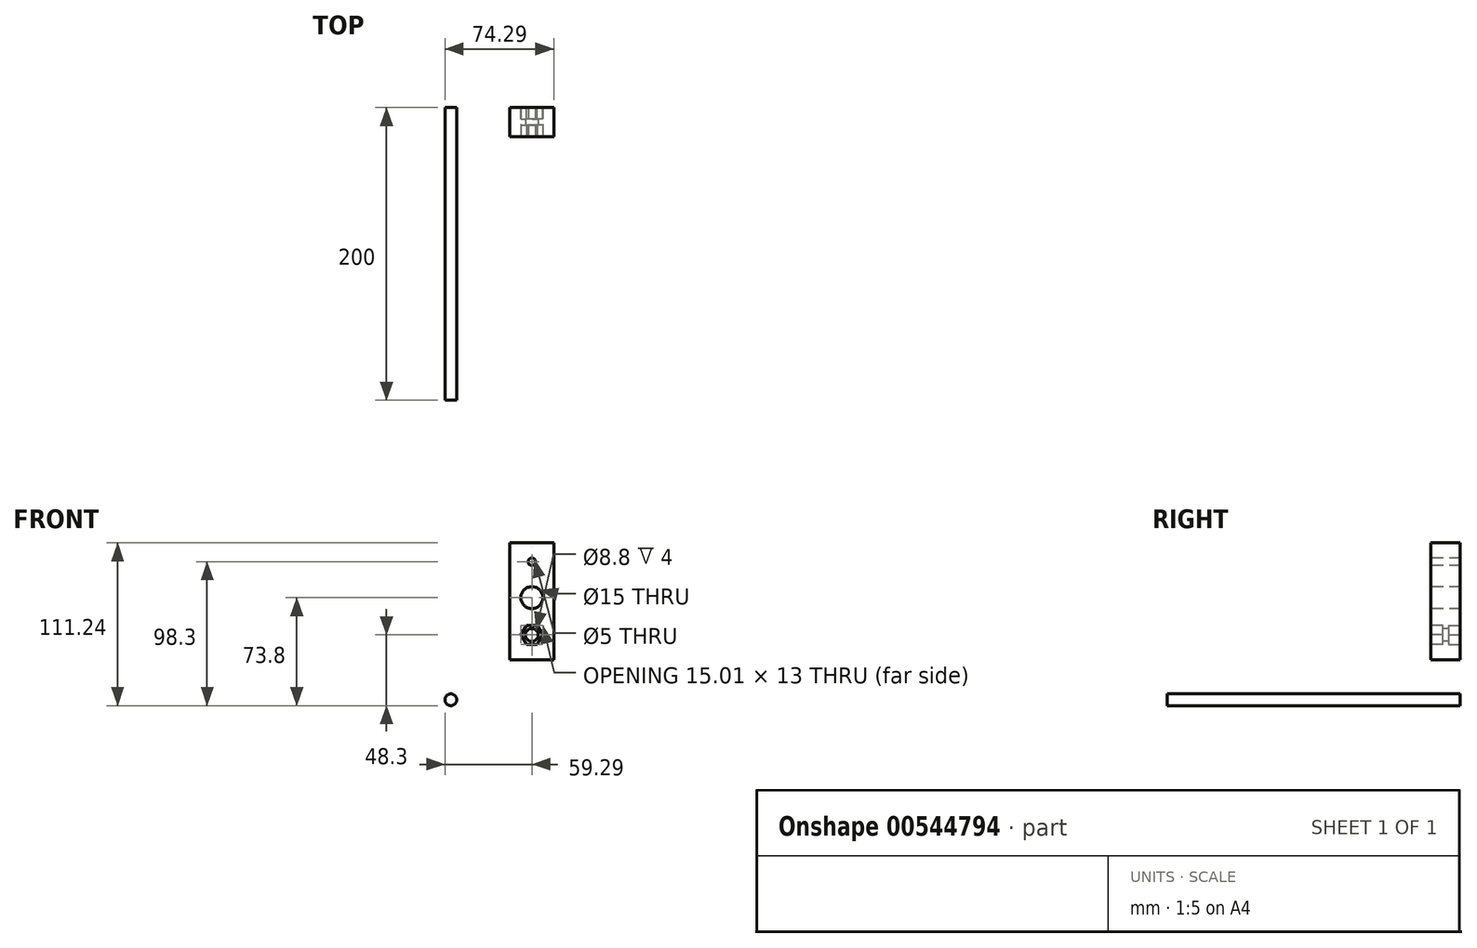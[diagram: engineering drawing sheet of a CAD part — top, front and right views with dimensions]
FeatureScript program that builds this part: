
annotation { "Feature Type Name" : "Feature", "Feature Type Description" : "" }
export const myFeature = defineFeature(function(context is Context, id is Id, definition is map)
    precondition{}
    {
        {
            var Q0;
            Q0=qCreatedBy(makeId("Front.planeOp"),FACE);
            var sketch = newSketch(context, id + "F0", { "sketchPlane" : qUnion([Q0])});
            skLineSegment(sketch, "E0.bottom", {"start": v(-15, 62.94) * mm, "end": v(15, 62.94) * mm});
            skLineSegment(sketch, "E0.top", {"start": v(-15, -17.06) * mm, "end": v(15, -17.06) * mm});
            skLineSegment(sketch, "E0.left", {"start": v(-15, 62.94) * mm, "end": v(-15, -17.06) * mm});
            skLineSegment(sketch, "E0.right", {"start": v(15, 62.94) * mm, "end": v(15, -17.06) * mm});
            skSolve(sketch);
        }
        {
            var Q0;
            Q0 = qSketchRegion(id + "F0", true);
            extrude(context, id + "F1", {"entities" : qUnion([Q0]), "depth" : 20 * mm, "offsetDistance" : 25 * mm});
        }
        {
            var Q0;
            Q0=makeQuery(id+"F1.opExtrude","CAP_FACE",FACE,{"disambiguationData":[OSD([sQuery(id+"F0.wireOp",EDGE,"E0.bottom"),sQuery(id+"F0.wireOp",EDGE,"E0.top"),sQuery(id+"F0.wireOp",EDGE,"E0.left"),sQuery(id+"F0.wireOp",EDGE,"E0.right")])],"isStart":false});
            var sketch = newSketch(context, id + "F2", { "sketchPlane" : qUnion([Q0])});
            skCircle(sketch, "E1.cCircle", {"center": v(0, 0) * mm, "radius": 6.5 * mm, "construction": true});
            skLineSegment(sketch, "E1.0", {"start": v(-3.75, 6.5) * mm, "end": v(3.75, 6.5) * mm});
            skLineSegment(sketch, "E1.1", {"start": v(3.75, 6.5) * mm, "end": v(7.5, 0) * mm});
            skLineSegment(sketch, "E1.2", {"start": v(7.5, 0) * mm, "end": v(3.75, -6.5) * mm});
            skLineSegment(sketch, "E1.3", {"start": v(3.75, -6.5) * mm, "end": v(-3.75, -6.5) * mm});
            skLineSegment(sketch, "E1.4", {"start": v(-3.75, -6.5) * mm, "end": v(-7.5, 0) * mm});
            skLineSegment(sketch, "E1.5", {"start": v(-7.5, 0) * mm, "end": v(-3.75, 6.5) * mm});
            skPoint(sketch, "E1.0.midPoint", {"position": v(0, 6.5) * mm});
            skSolve(sketch);
        }
        {
            var Q0;
            Q0 = qSketchRegion(id + "F2", true);
            extrude(context, id + "F3", {"entities" : qUnion([Q0]), "operationType" : NewBodyOperationType.REMOVE, "oppositeDirection" : true, "depth" : 8 * mm, "offsetDistance" : 25 * mm});
        }
        {
            var Q0;
            Q0=makeQuery(id+"F3.boolean.opBoolean","COPY",FACE,{"derivedFrom":makeQuery(id+"F3.opExtrude","CAP_FACE",FACE,{"disambiguationData":[OSD([sQuery(id+"F2.wireOp",EDGE,"E1.0"),sQuery(id+"F2.wireOp",EDGE,"E1.1"),sQuery(id+"F2.wireOp",EDGE,"E1.2"),sQuery(id+"F2.wireOp",EDGE,"E1.3"),sQuery(id+"F2.wireOp",EDGE,"E1.4"),sQuery(id+"F2.wireOp",EDGE,"E1.5")])],"isStart":false})});
            var sketch = newSketch(context, id + "F4", { "sketchPlane" : qUnion([Q0])});
            skPoint(sketch, "E2", {"position": v(0, 0) * mm});
            skSolve(sketch);
        }
        {
            var Q0;
            Q0=sQuery(id+"F4.wireOp",VERTEX,"E2");
            var Q1;
            Q1=makeQuery(id+"F1.opExtrude","SWEPT_BODY",BODY,{"disambiguationData":[OSD([sQuery(id+"F0.wireOp",EDGE,"E0.bottom"),sQuery(id+"F0.wireOp",EDGE,"E0.top"),sQuery(id+"F0.wireOp",EDGE,"E0.left"),sQuery(id+"F0.wireOp",EDGE,"E0.right")])]});
            hole(context, id + "F5", {"style" : HoleStyle.SIMPLE, "endStyle" : HoleEndStyle.THROUGH, "standardTappedOrClearance" : lookupTablePath({ "standard" : "ISO", "fit" : "Normal", "size" : "M8", "type" : "Clearance" }), "standardBlindInLast" : lookupTablePath({ "fit" : "Standard", "standard" : "ISO", "size" : "M8", "type" : "Clearance" }), "holeDiameter" : 8.8 * mm, "isTappedThrough" : true, "tappedDepth" : 12 * mm, "tapClearance" : 3, "startFromSketch" : true, "locations" : qUnion([Q0]), "scope" : qUnion([Q1])});
        }
        {
            var Q0;
            Q0=makeQuery(id+"F1.opExtrude","CAP_FACE",FACE,{"disambiguationData":[OSD([sQuery(id+"F0.wireOp",EDGE,"E0.bottom"),sQuery(id+"F0.wireOp",EDGE,"E0.top"),sQuery(id+"F0.wireOp",EDGE,"E0.left"),sQuery(id+"F0.wireOp",EDGE,"E0.right")])],"isStart":true});
            var sketch = newSketch(context, id + "F6", { "sketchPlane" : qUnion([Q0])});
            skCircle(sketch, "E3.cCircle", {"center": v(0, 0) * mm, "radius": 6.5 * mm, "construction": true});
            skLineSegment(sketch, "E3.0", {"start": v(7.5, 0) * mm, "end": v(3.75, -6.5) * mm});
            skLineSegment(sketch, "E3.1", {"start": v(3.75, -6.5) * mm, "end": v(-3.75, -6.5) * mm});
            skLineSegment(sketch, "E3.2", {"start": v(-3.75, -6.5) * mm, "end": v(-7.5, 0) * mm});
            skLineSegment(sketch, "E3.3", {"start": v(-7.5, 0) * mm, "end": v(-3.75, 6.5) * mm});
            skLineSegment(sketch, "E3.4", {"start": v(-3.75, 6.5) * mm, "end": v(3.75, 6.5) * mm});
            skLineSegment(sketch, "E3.5", {"start": v(3.75, 6.5) * mm, "end": v(7.5, 0) * mm});
            skPoint(sketch, "E3.0.midPoint", {"position": v(5.63, -3.25) * mm});
            skSolve(sketch);
        }
        {
            var Q0;
            Q0 = qSketchRegion(id + "F6", true);
            extrude(context, id + "F7", {"entities" : qUnion([Q0]), "operationType" : NewBodyOperationType.REMOVE, "oppositeDirection" : true, "depth" : 8 * mm, "offsetDistance" : 25 * mm});
        }
        {
            var Q0;
            Q0=qCreatedBy(makeId("Front.planeOp"),FACE);
            var sketch = newSketch(context, id + "F8", { "sketchPlane" : qUnion([Q0])});
            skCircle(sketch, "E4", {"center": v(-55.29, -44.3) * mm, "radius": 4 * mm});
            skSolve(sketch);
        }
        {
            var Q0;
            Q0 = qSketchRegion(id + "F8", true);
            extrude(context, id + "F9", {"entities" : qUnion([Q0]), "depth" : 200 * mm, "offsetDistance" : 25 * mm});
        }
        {
            var Q0;
            Q0=makeQuery(id+"F1.opExtrude","CAP_FACE",FACE,{"disambiguationData":[OSD([sQuery(id+"F0.wireOp",EDGE,"E0.bottom"),sQuery(id+"F0.wireOp",EDGE,"E0.top"),sQuery(id+"F0.wireOp",EDGE,"E0.left"),sQuery(id+"F0.wireOp",EDGE,"E0.right")])],"isStart":false});
            var sketch = newSketch(context, id + "F10", { "sketchPlane" : qUnion([Q0])});
            skPoint(sketch, "E5", {"position": v(0, 25.5) * mm});
            skSolve(sketch);
        }
        {
            var Q0;
            Q0=sQuery(id+"F10.wireOp",VERTEX,"E5");
            var Q1;
            Q1=makeQuery(id+"F1.opExtrude","SWEPT_BODY",BODY,{"disambiguationData":[OSD([sQuery(id+"F0.wireOp",EDGE,"E0.bottom"),sQuery(id+"F0.wireOp",EDGE,"E0.top"),sQuery(id+"F0.wireOp",EDGE,"E0.left"),sQuery(id+"F0.wireOp",EDGE,"E0.right")])]});
            hole(context, id + "F11", {"style" : HoleStyle.SIMPLE, "endStyle" : HoleEndStyle.THROUGH, "holeDiameter" : 15 * mm, "isTappedThrough" : true, "tappedDepth" : 12 * mm, "tapClearance" : 3, "startFromSketch" : true, "locations" : qUnion([Q0]), "scope" : qUnion([Q1])});
        }
        {
            var Q0;
            Q0=makeQuery(id+"F1.opExtrude","CAP_FACE",FACE,{"disambiguationData":[OSD([sQuery(id+"F0.wireOp",EDGE,"E0.bottom"),sQuery(id+"F0.wireOp",EDGE,"E0.top"),sQuery(id+"F0.wireOp",EDGE,"E0.left"),sQuery(id+"F0.wireOp",EDGE,"E0.right")])],"isStart":false});
            var sketch = newSketch(context, id + "F12", { "sketchPlane" : qUnion([Q0])});
            skPoint(sketch, "E6", {"position": v(0, 50) * mm});
            skSolve(sketch);
        }
        {
            var Q0;
            Q0=sQuery(id+"F12.wireOp",VERTEX,"E6");
            var Q1;
            Q1=makeQuery(id+"F1.opExtrude","SWEPT_BODY",BODY,{"disambiguationData":[OSD([sQuery(id+"F0.wireOp",EDGE,"E0.bottom"),sQuery(id+"F0.wireOp",EDGE,"E0.top"),sQuery(id+"F0.wireOp",EDGE,"E0.left"),sQuery(id+"F0.wireOp",EDGE,"E0.right")])]});
            hole(context, id + "F13", {"style" : HoleStyle.SIMPLE, "endStyle" : HoleEndStyle.THROUGH, "holeDiameter" : 5 * mm, "isTappedThrough" : true, "tappedDepth" : 12 * mm, "tapClearance" : 3, "locations" : qUnion([Q0]), "scope" : qUnion([Q1])});
        }
    });
